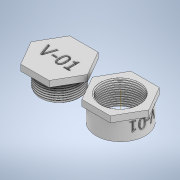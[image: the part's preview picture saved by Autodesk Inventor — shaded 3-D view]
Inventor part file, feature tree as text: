
AUTODESK INVENTOR PART (.ipt)
format: ipt  version: 2021.1 (Build 251245000, 245)  size: 862,720 bytes
history: native  units: in
note: dims shown in document units (in); Inventor stores cm internally (conversion verified against a paired STEP export)
features: sketch x9, extrude x6, helix x2, plane x1, other x1
ambient origin geometry x8: Origin, YZ Plane, XZ Plane, XY Plane, X Axis, Y Axis, Z Axis, Center Point
bodies: Body1 (feature_tree)
feature tree (19):
  extrude  "NutShaft"  Depth=1.0in
  helix  "CoilForNut"  [1 undecoded]
  extrude  "BoltHexHead"  Depth=0.0045in
  extrude  "BoltShaft"  Depth=0.0833in
  helix  "CoilForBolt"  [1 undecoded]
  extrude  "EmbossForBolt"  Depth=2.5in
  plane  "Work Plane4"
  other  "EmbossForNut"
  extrude  "NutHexHead"  Depth=0.25in
  extrude  "HoleForBolt"  Depth=0.75in TaperAngle=0.0deg
  sketch  "Sketch4"  dims[d4=2.0in d5=1.5438in d6=1.0in d7=0.0in]
  sketch  "Sketch6"  dims[d33=60.0deg d35=0.0045in]
  sketch  "Sketch7"  dims[d36=0.8174in d37=0.0833in d38=0.0833in]
  sketch  "Sketch8"  dims[d39=1.2in d40=0.3937in d41=0.0in d42=90.0deg d43=90.0deg d44=0.0in d45=0.0in d46=2.5in]
  sketch  "Sketch9"  dims[d47=0.25in d48=0.0in d49=1.6175in]
  sketch  "Sketch11"  dims[d50=2.0in d51=0.75in d52=0.0in]
  sketch  "Sketch12"  dims[d53=60.0deg]
  sketch  "Sketch13"  dims[d54=0.0074in]
  sketch  "Sketch14"  dims[d56=0.8087in d57=0.7569in d58=0.0833in d59=1.0in d60=0.3937in d61=0.0in d62=90.0deg d63=90.0deg d64=0.0in d65=0.0in d66=0.0833in d68=0.1in d69=0.0in d70=1.0in d71=0.1in d72=0.0in d73=2.0in d74=0.25in d75=0.0in d76=0.75in d77=0.0in]
note: 2 required parameter values undecoded (feature->parameter linkage not recoverable at this tier; creation-order binding heuristic only, values carry confidence <= 0.55)
